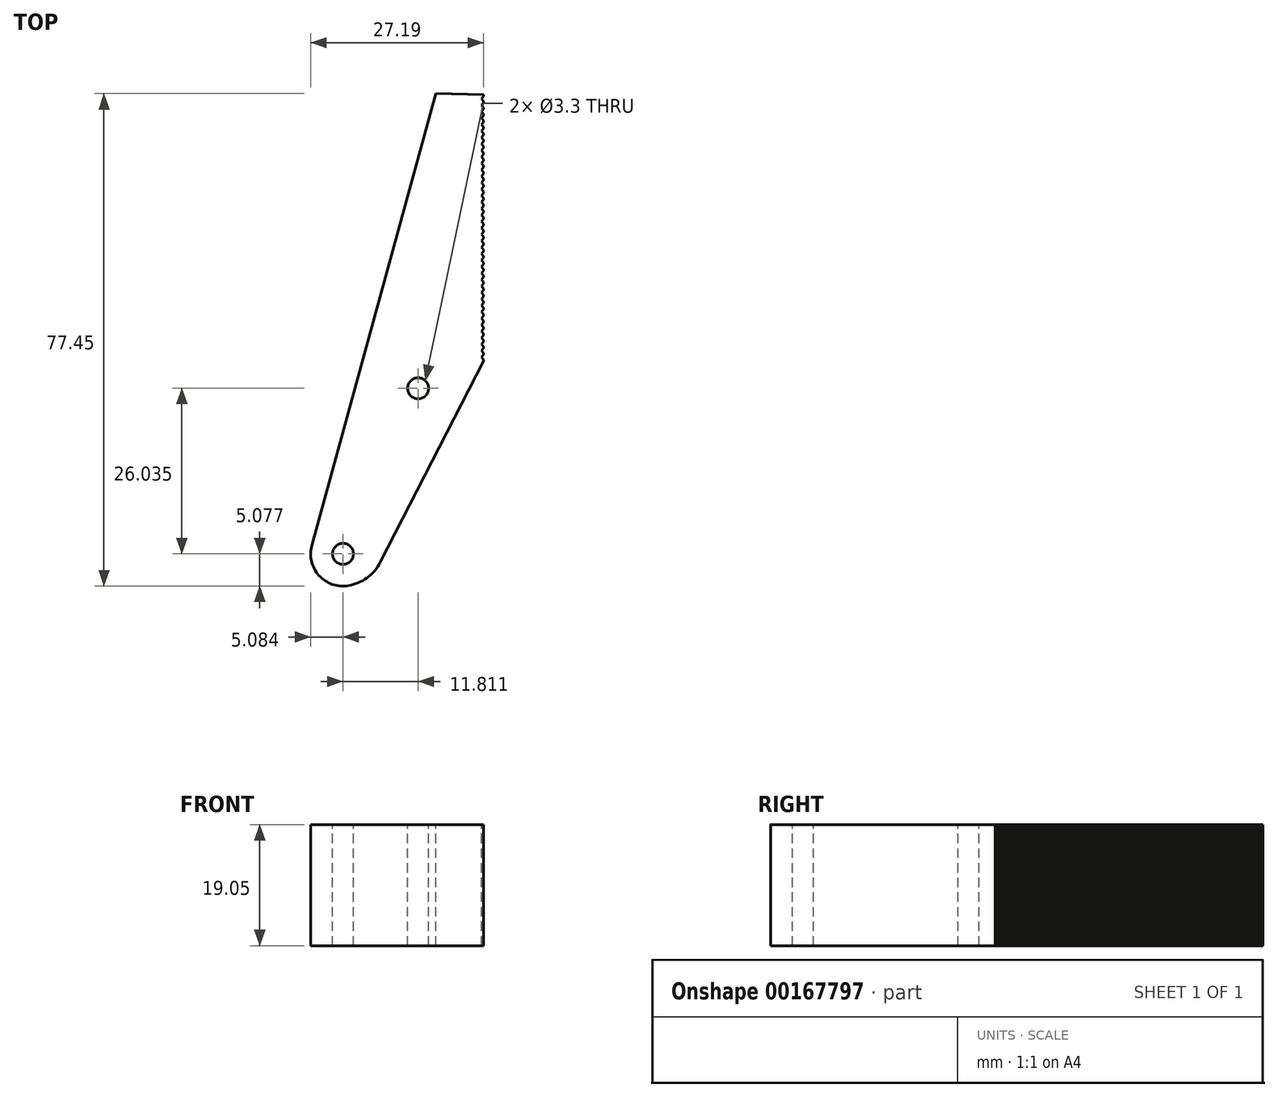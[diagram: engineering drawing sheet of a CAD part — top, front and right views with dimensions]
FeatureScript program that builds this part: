
annotation { "Feature Type Name" : "Feature", "Feature Type Description" : "" }
export const myFeature = defineFeature(function(context is Context, id is Id, definition is map)
    precondition{}
    {
        {
            var Q0;
            Q0=qCreatedBy(makeId("Top.planeOp"),FACE);
            var sketch = newSketch(context, id + "F0", { "sketchPlane" : qUnion([Q0])});
            skLineSegment(sketch, "E0", {"start": v(19.05, 0) * mm, "end": v(19.05, 63.5) * mm});
            skLineSegment(sketch, "E1", {"start": v(19.05, 0) * mm, "end": v(2.8, -31.63) * mm});
            skLineSegment(sketch, "E2", {"start": v(19.05, 63.5) * mm, "end": v(17.46, 63.5) * mm});
            skLineSegment(sketch, "E3", {"start": v(17.46, 63.5) * mm, "end": v(0, 0) * mm});
            skLineSegment(sketch, "E4", {"start": v(0, 0) * mm, "end": v(-8.94, -32.52) * mm});
            skArc(sketch, "E5", {"start": v(-8.94, -32.52) * mm, "mid": v(-2.82, -35.36) * mm, "end": v(2.8, -31.63) * mm});
            skSolve(sketch);
        }
        {
            var Q0;
            Q0 = qSketchRegion(id + "F0", true);
            extrude(context, id + "F1", {"entities" : qUnion([Q0]), "depth" : 19.05 * mm});
        }
        {
            var Q0;
            Q0=makeQuery(id+"F1.opExtrude","CAP_FACE",FACE,{"disambiguationData":[OSD([sQuery(id+"F0.wireOp",EDGE,"E0"),sQuery(id+"F0.wireOp",EDGE,"V7W4c1gP-l52r-vqxn-igbG-do98eLeIA0Zb"),sQuery(id+"F0.wireOp",EDGE,"MUQwh4st-e7uD-OgjB-epZt-JrECyby666Zu"),sQuery(id+"F0.wireOp",EDGE,"E1"),sQuery(id+"F0.wireOp",EDGE,"YxZZfRpB-2lz4-PjBK-BrxY-fdydKXbAcn2m")])],"isStart":false});
            var sketch = newSketch(context, id + "F2", { "sketchPlane" : qUnion([Q0])});
            skLineSegment(sketch, "E6", {"start": v(19.05, 0.25) * mm, "end": v(18.71, 0.64) * mm});
            skLineSegment(sketch, "E7", {"start": v(18.71, 0.64) * mm, "end": v(19.05, 1.02) * mm});
            skLineSegment(sketch, "E8", {"start": v(19.05, 1.02) * mm, "end": v(19.05, 0.25) * mm});
            skLineSegment(sketch, "E9.0.1.0", {"start": v(18.71, 1.65) * mm, "end": v(19.05, 2.03) * mm});
            skLineSegment(sketch, "E9.0.1.1", {"start": v(19.05, 2.03) * mm, "end": v(19.05, 1.27) * mm});
            skLineSegment(sketch, "E9.0.1.2", {"start": v(19.05, 1.27) * mm, "end": v(18.71, 1.65) * mm});
            skLineSegment(sketch, "E9.0.2.0", {"start": v(18.71, 2.67) * mm, "end": v(19.05, 3.05) * mm});
            skLineSegment(sketch, "E9.0.2.1", {"start": v(19.05, 3.05) * mm, "end": v(19.05, 2.29) * mm});
            skLineSegment(sketch, "E9.0.2.2", {"start": v(19.05, 2.29) * mm, "end": v(18.71, 2.67) * mm});
            skLineSegment(sketch, "E9.0.3.0", {"start": v(18.71, 3.68) * mm, "end": v(19.05, 4.06) * mm});
            skLineSegment(sketch, "E9.0.3.1", {"start": v(19.05, 4.06) * mm, "end": v(19.05, 3.3) * mm});
            skLineSegment(sketch, "E9.0.3.2", {"start": v(19.05, 3.3) * mm, "end": v(18.71, 3.68) * mm});
            skLineSegment(sketch, "E9.0.4.0", {"start": v(18.71, 4.7) * mm, "end": v(19.05, 5.08) * mm});
            skLineSegment(sketch, "E9.0.4.1", {"start": v(19.05, 5.08) * mm, "end": v(19.05, 4.32) * mm});
            skLineSegment(sketch, "E9.0.4.2", {"start": v(19.05, 4.32) * mm, "end": v(18.71, 4.7) * mm});
            skLineSegment(sketch, "E9.0.5.0", {"start": v(18.71, 5.72) * mm, "end": v(19.05, 6.1) * mm});
            skLineSegment(sketch, "E9.0.5.1", {"start": v(19.05, 6.1) * mm, "end": v(19.05, 5.33) * mm});
            skLineSegment(sketch, "E9.0.5.2", {"start": v(19.05, 5.33) * mm, "end": v(18.71, 5.72) * mm});
            skLineSegment(sketch, "E9.0.6.0", {"start": v(18.71, 6.73) * mm, "end": v(19.05, 7.11) * mm});
            skLineSegment(sketch, "E9.0.6.1", {"start": v(19.05, 7.11) * mm, "end": v(19.05, 6.35) * mm});
            skLineSegment(sketch, "E9.0.6.2", {"start": v(19.05, 6.35) * mm, "end": v(18.71, 6.73) * mm});
            skLineSegment(sketch, "E9.0.7.0", {"start": v(18.71, 7.75) * mm, "end": v(19.05, 8.13) * mm});
            skLineSegment(sketch, "E9.0.7.1", {"start": v(19.05, 8.13) * mm, "end": v(19.05, 7.37) * mm});
            skLineSegment(sketch, "E9.0.7.2", {"start": v(19.05, 7.37) * mm, "end": v(18.71, 7.75) * mm});
            skLineSegment(sketch, "E9.0.8.0", {"start": v(18.71, 8.76) * mm, "end": v(19.05, 9.14) * mm});
            skLineSegment(sketch, "E9.0.8.1", {"start": v(19.05, 9.14) * mm, "end": v(19.05, 8.38) * mm});
            skLineSegment(sketch, "E9.0.8.2", {"start": v(19.05, 8.38) * mm, "end": v(18.71, 8.76) * mm});
            skLineSegment(sketch, "E9.0.9.0", {"start": v(18.71, 9.78) * mm, "end": v(19.05, 10.16) * mm});
            skLineSegment(sketch, "E9.0.9.1", {"start": v(19.05, 10.16) * mm, "end": v(19.05, 9.4) * mm});
            skLineSegment(sketch, "E9.0.9.2", {"start": v(19.05, 9.4) * mm, "end": v(18.71, 9.78) * mm});
            skLineSegment(sketch, "E9.0.10.0", {"start": v(18.71, 10.8) * mm, "end": v(19.05, 11.18) * mm});
            skLineSegment(sketch, "E9.0.10.1", {"start": v(19.05, 11.18) * mm, "end": v(19.05, 10.41) * mm});
            skLineSegment(sketch, "E9.0.10.2", {"start": v(19.05, 10.41) * mm, "end": v(18.71, 10.8) * mm});
            skLineSegment(sketch, "E9.direction1", {"start": v(19.05, 0.25) * mm, "end": v(44.45, 0.25) * mm, "construction": true});
            skLineSegment(sketch, "E9.direction2", {"start": v(19.05, 0.25) * mm, "end": v(19.05, 1.27) * mm, "construction": true});
            skLineSegment(sketch, "E10.0.0.11", {"start": v(18.71, 11.81) * mm, "end": v(19.05, 12.2) * mm});
            skLineSegment(sketch, "E10.3.0.11", {"start": v(19.05, 12.2) * mm, "end": v(19.05, 11.43) * mm});
            skLineSegment(sketch, "E10.6.0.11", {"start": v(19.05, 11.43) * mm, "end": v(18.71, 11.81) * mm});
            skLineSegment(sketch, "E10.0.0.12", {"start": v(18.71, 12.83) * mm, "end": v(19.05, 13.2) * mm});
            skLineSegment(sketch, "E10.3.0.12", {"start": v(19.05, 13.2) * mm, "end": v(19.05, 12.45) * mm});
            skLineSegment(sketch, "E10.6.0.12", {"start": v(19.05, 12.45) * mm, "end": v(18.71, 12.83) * mm});
            skLineSegment(sketch, "E10.0.0.13", {"start": v(18.71, 13.84) * mm, "end": v(19.05, 14.22) * mm});
            skLineSegment(sketch, "E10.3.0.13", {"start": v(19.05, 14.22) * mm, "end": v(19.05, 13.46) * mm});
            skLineSegment(sketch, "E10.6.0.13", {"start": v(19.05, 13.46) * mm, "end": v(18.71, 13.84) * mm});
            skLineSegment(sketch, "E10.0.0.14", {"start": v(18.71, 14.86) * mm, "end": v(19.05, 15.24) * mm});
            skLineSegment(sketch, "E10.3.0.14", {"start": v(19.05, 15.24) * mm, "end": v(19.05, 14.48) * mm});
            skLineSegment(sketch, "E10.6.0.14", {"start": v(19.05, 14.48) * mm, "end": v(18.71, 14.86) * mm});
            skLineSegment(sketch, "E10.0.0.15", {"start": v(18.71, 15.88) * mm, "end": v(19.05, 16.26) * mm});
            skLineSegment(sketch, "E10.3.0.15", {"start": v(19.05, 16.26) * mm, "end": v(19.05, 15.5) * mm});
            skLineSegment(sketch, "E10.6.0.15", {"start": v(19.05, 15.5) * mm, "end": v(18.71, 15.88) * mm});
            skLineSegment(sketch, "E10.0.0.16", {"start": v(18.71, 16.9) * mm, "end": v(19.05, 17.27) * mm});
            skLineSegment(sketch, "E10.3.0.16", {"start": v(19.05, 17.27) * mm, "end": v(19.05, 16.51) * mm});
            skLineSegment(sketch, "E10.6.0.16", {"start": v(19.05, 16.51) * mm, "end": v(18.71, 16.9) * mm});
            skLineSegment(sketch, "E10.0.0.17", {"start": v(18.71, 17.9) * mm, "end": v(19.05, 18.29) * mm});
            skLineSegment(sketch, "E10.3.0.17", {"start": v(19.05, 18.29) * mm, "end": v(19.05, 17.53) * mm});
            skLineSegment(sketch, "E10.6.0.17", {"start": v(19.05, 17.53) * mm, "end": v(18.71, 17.9) * mm});
            skLineSegment(sketch, "E10.0.0.18", {"start": v(18.71, 18.92) * mm, "end": v(19.05, 19.3) * mm});
            skLineSegment(sketch, "E10.3.0.18", {"start": v(19.05, 19.3) * mm, "end": v(19.05, 18.54) * mm});
            skLineSegment(sketch, "E10.6.0.18", {"start": v(19.05, 18.54) * mm, "end": v(18.71, 18.92) * mm});
            skLineSegment(sketch, "E10.0.0.19", {"start": v(18.71, 19.94) * mm, "end": v(19.05, 20.32) * mm});
            skLineSegment(sketch, "E10.3.0.19", {"start": v(19.05, 20.32) * mm, "end": v(19.05, 19.56) * mm});
            skLineSegment(sketch, "E10.6.0.19", {"start": v(19.05, 19.56) * mm, "end": v(18.71, 19.94) * mm});
            skLineSegment(sketch, "E10.0.0.20", {"start": v(18.71, 20.96) * mm, "end": v(19.05, 21.34) * mm});
            skLineSegment(sketch, "E10.3.0.20", {"start": v(19.05, 21.34) * mm, "end": v(19.05, 20.57) * mm});
            skLineSegment(sketch, "E10.6.0.20", {"start": v(19.05, 20.57) * mm, "end": v(18.71, 20.96) * mm});
            skLineSegment(sketch, "E10.0.0.21", {"start": v(18.71, 21.97) * mm, "end": v(19.05, 22.35) * mm});
            skLineSegment(sketch, "E10.3.0.21", {"start": v(19.05, 22.35) * mm, "end": v(19.05, 21.6) * mm});
            skLineSegment(sketch, "E10.6.0.21", {"start": v(19.05, 21.6) * mm, "end": v(18.71, 21.97) * mm});
            skLineSegment(sketch, "E10.0.0.22", {"start": v(18.71, 22.99) * mm, "end": v(19.05, 23.37) * mm});
            skLineSegment(sketch, "E10.3.0.22", {"start": v(19.05, 23.37) * mm, "end": v(19.05, 22.6) * mm});
            skLineSegment(sketch, "E10.6.0.22", {"start": v(19.05, 22.6) * mm, "end": v(18.71, 22.99) * mm});
            skLineSegment(sketch, "E10.0.0.23", {"start": v(18.71, 24) * mm, "end": v(19.05, 24.38) * mm});
            skLineSegment(sketch, "E10.3.0.23", {"start": v(19.05, 24.38) * mm, "end": v(19.05, 23.62) * mm});
            skLineSegment(sketch, "E10.6.0.23", {"start": v(19.05, 23.62) * mm, "end": v(18.71, 24) * mm});
            skLineSegment(sketch, "E10.0.0.24", {"start": v(18.71, 25.02) * mm, "end": v(19.05, 25.4) * mm});
            skLineSegment(sketch, "E10.3.0.24", {"start": v(19.05, 25.4) * mm, "end": v(19.05, 24.64) * mm});
            skLineSegment(sketch, "E10.6.0.24", {"start": v(19.05, 24.64) * mm, "end": v(18.71, 25.02) * mm});
            skLineSegment(sketch, "E10.0.0.25", {"start": v(18.71, 26.04) * mm, "end": v(19.05, 26.42) * mm});
            skLineSegment(sketch, "E10.3.0.25", {"start": v(19.05, 26.42) * mm, "end": v(19.05, 25.65) * mm});
            skLineSegment(sketch, "E10.6.0.25", {"start": v(19.05, 25.65) * mm, "end": v(18.71, 26.04) * mm});
            skLineSegment(sketch, "E10.0.0.26", {"start": v(18.71, 27.05) * mm, "end": v(19.05, 27.43) * mm});
            skLineSegment(sketch, "E10.3.0.26", {"start": v(19.05, 27.43) * mm, "end": v(19.05, 26.67) * mm});
            skLineSegment(sketch, "E10.6.0.26", {"start": v(19.05, 26.67) * mm, "end": v(18.71, 27.05) * mm});
            skLineSegment(sketch, "E10.0.0.27", {"start": v(18.71, 28.07) * mm, "end": v(19.05, 28.45) * mm});
            skLineSegment(sketch, "E10.3.0.27", {"start": v(19.05, 28.45) * mm, "end": v(19.05, 27.69) * mm});
            skLineSegment(sketch, "E10.6.0.27", {"start": v(19.05, 27.69) * mm, "end": v(18.71, 28.07) * mm});
            skLineSegment(sketch, "E10.0.0.28", {"start": v(18.71, 29.08) * mm, "end": v(19.05, 29.46) * mm});
            skLineSegment(sketch, "E10.3.0.28", {"start": v(19.05, 29.46) * mm, "end": v(19.05, 28.7) * mm});
            skLineSegment(sketch, "E10.6.0.28", {"start": v(19.05, 28.7) * mm, "end": v(18.71, 29.08) * mm});
            skLineSegment(sketch, "E10.0.0.29", {"start": v(18.71, 30.1) * mm, "end": v(19.05, 30.48) * mm});
            skLineSegment(sketch, "E10.3.0.29", {"start": v(19.05, 30.48) * mm, "end": v(19.05, 29.72) * mm});
            skLineSegment(sketch, "E10.6.0.29", {"start": v(19.05, 29.72) * mm, "end": v(18.71, 30.1) * mm});
            skLineSegment(sketch, "E10.0.0.30", {"start": v(18.71, 31.12) * mm, "end": v(19.05, 31.5) * mm});
            skLineSegment(sketch, "E10.3.0.30", {"start": v(19.05, 31.5) * mm, "end": v(19.05, 30.73) * mm});
            skLineSegment(sketch, "E10.6.0.30", {"start": v(19.05, 30.73) * mm, "end": v(18.71, 31.12) * mm});
            skLineSegment(sketch, "E10.0.0.31", {"start": v(18.71, 32.13) * mm, "end": v(19.05, 32.51) * mm});
            skLineSegment(sketch, "E10.3.0.31", {"start": v(19.05, 32.51) * mm, "end": v(19.05, 31.75) * mm});
            skLineSegment(sketch, "E10.6.0.31", {"start": v(19.05, 31.75) * mm, "end": v(18.71, 32.13) * mm});
            skLineSegment(sketch, "E10.0.0.32", {"start": v(18.71, 33.15) * mm, "end": v(19.05, 33.53) * mm});
            skLineSegment(sketch, "E10.3.0.32", {"start": v(19.05, 33.53) * mm, "end": v(19.05, 32.77) * mm});
            skLineSegment(sketch, "E10.6.0.32", {"start": v(19.05, 32.77) * mm, "end": v(18.71, 33.15) * mm});
            skLineSegment(sketch, "E10.0.0.33", {"start": v(18.71, 34.16) * mm, "end": v(19.05, 34.54) * mm});
            skLineSegment(sketch, "E10.3.0.33", {"start": v(19.05, 34.54) * mm, "end": v(19.05, 33.78) * mm});
            skLineSegment(sketch, "E10.6.0.33", {"start": v(19.05, 33.78) * mm, "end": v(18.71, 34.16) * mm});
            skLineSegment(sketch, "E10.0.0.34", {"start": v(18.71, 35.18) * mm, "end": v(19.05, 35.56) * mm});
            skLineSegment(sketch, "E10.3.0.34", {"start": v(19.05, 35.56) * mm, "end": v(19.05, 34.8) * mm});
            skLineSegment(sketch, "E10.6.0.34", {"start": v(19.05, 34.8) * mm, "end": v(18.71, 35.18) * mm});
            skLineSegment(sketch, "E10.0.0.35", {"start": v(18.71, 36.2) * mm, "end": v(19.05, 36.58) * mm});
            skLineSegment(sketch, "E10.3.0.35", {"start": v(19.05, 36.58) * mm, "end": v(19.05, 35.81) * mm});
            skLineSegment(sketch, "E10.6.0.35", {"start": v(19.05, 35.81) * mm, "end": v(18.71, 36.2) * mm});
            skLineSegment(sketch, "E10.0.0.36", {"start": v(18.71, 37.21) * mm, "end": v(19.05, 37.6) * mm});
            skLineSegment(sketch, "E10.3.0.36", {"start": v(19.05, 37.6) * mm, "end": v(19.05, 36.83) * mm});
            skLineSegment(sketch, "E10.6.0.36", {"start": v(19.05, 36.83) * mm, "end": v(18.71, 37.21) * mm});
            skLineSegment(sketch, "E10.0.0.37", {"start": v(18.71, 38.23) * mm, "end": v(19.05, 38.6) * mm});
            skLineSegment(sketch, "E10.3.0.37", {"start": v(19.05, 38.6) * mm, "end": v(19.05, 37.85) * mm});
            skLineSegment(sketch, "E10.6.0.37", {"start": v(19.05, 37.85) * mm, "end": v(18.71, 38.23) * mm});
            skLineSegment(sketch, "E10.0.0.38", {"start": v(18.71, 39.24) * mm, "end": v(19.05, 39.62) * mm});
            skLineSegment(sketch, "E10.3.0.38", {"start": v(19.05, 39.62) * mm, "end": v(19.05, 38.86) * mm});
            skLineSegment(sketch, "E10.6.0.38", {"start": v(19.05, 38.86) * mm, "end": v(18.71, 39.24) * mm});
            skLineSegment(sketch, "E10.0.0.39", {"start": v(18.71, 40.26) * mm, "end": v(19.05, 40.64) * mm});
            skLineSegment(sketch, "E10.3.0.39", {"start": v(19.05, 40.64) * mm, "end": v(19.05, 39.88) * mm});
            skLineSegment(sketch, "E10.6.0.39", {"start": v(19.05, 39.88) * mm, "end": v(18.71, 40.26) * mm});
            skLineSegment(sketch, "E11.0.0.40", {"start": v(18.71, 41.28) * mm, "end": v(19.05, 41.66) * mm});
            skLineSegment(sketch, "E11.3.0.40", {"start": v(19.05, 41.66) * mm, "end": v(19.05, 40.9) * mm});
            skLineSegment(sketch, "E11.6.0.40", {"start": v(19.05, 40.9) * mm, "end": v(18.71, 41.28) * mm});
            skLineSegment(sketch, "E11.0.0.41", {"start": v(18.71, 42.3) * mm, "end": v(19.05, 42.67) * mm});
            skLineSegment(sketch, "E11.3.0.41", {"start": v(19.05, 42.67) * mm, "end": v(19.05, 41.91) * mm});
            skLineSegment(sketch, "E11.6.0.41", {"start": v(19.05, 41.91) * mm, "end": v(18.71, 42.3) * mm});
            skLineSegment(sketch, "E11.0.0.42", {"start": v(18.71, 43.3) * mm, "end": v(19.05, 43.69) * mm});
            skLineSegment(sketch, "E11.3.0.42", {"start": v(19.05, 43.69) * mm, "end": v(19.05, 42.93) * mm});
            skLineSegment(sketch, "E11.6.0.42", {"start": v(19.05, 42.93) * mm, "end": v(18.71, 43.3) * mm});
            skLineSegment(sketch, "E11.0.0.43", {"start": v(18.71, 44.32) * mm, "end": v(19.05, 44.7) * mm});
            skLineSegment(sketch, "E11.3.0.43", {"start": v(19.05, 44.7) * mm, "end": v(19.05, 43.94) * mm});
            skLineSegment(sketch, "E11.6.0.43", {"start": v(19.05, 43.94) * mm, "end": v(18.71, 44.32) * mm});
            skLineSegment(sketch, "E11.0.0.44", {"start": v(18.71, 45.34) * mm, "end": v(19.05, 45.72) * mm});
            skLineSegment(sketch, "E11.3.0.44", {"start": v(19.05, 45.72) * mm, "end": v(19.05, 44.96) * mm});
            skLineSegment(sketch, "E11.6.0.44", {"start": v(19.05, 44.96) * mm, "end": v(18.71, 45.34) * mm});
            skLineSegment(sketch, "E11.0.0.45", {"start": v(18.71, 46.36) * mm, "end": v(19.05, 46.74) * mm});
            skLineSegment(sketch, "E11.3.0.45", {"start": v(19.05, 46.74) * mm, "end": v(19.05, 45.97) * mm});
            skLineSegment(sketch, "E11.6.0.45", {"start": v(19.05, 45.97) * mm, "end": v(18.71, 46.36) * mm});
            skLineSegment(sketch, "E11.0.0.46", {"start": v(18.71, 47.37) * mm, "end": v(19.05, 47.75) * mm});
            skLineSegment(sketch, "E11.3.0.46", {"start": v(19.05, 47.75) * mm, "end": v(19.05, 47) * mm});
            skLineSegment(sketch, "E11.6.0.46", {"start": v(19.05, 47) * mm, "end": v(18.71, 47.37) * mm});
            skLineSegment(sketch, "E11.0.0.47", {"start": v(18.71, 48.39) * mm, "end": v(19.05, 48.77) * mm});
            skLineSegment(sketch, "E11.3.0.47", {"start": v(19.05, 48.77) * mm, "end": v(19.05, 48) * mm});
            skLineSegment(sketch, "E11.6.0.47", {"start": v(19.05, 48) * mm, "end": v(18.71, 48.39) * mm});
            skLineSegment(sketch, "E11.0.0.48", {"start": v(18.71, 49.4) * mm, "end": v(19.05, 49.78) * mm});
            skLineSegment(sketch, "E11.3.0.48", {"start": v(19.05, 49.78) * mm, "end": v(19.05, 49.02) * mm});
            skLineSegment(sketch, "E11.6.0.48", {"start": v(19.05, 49.02) * mm, "end": v(18.71, 49.4) * mm});
            skLineSegment(sketch, "E11.0.0.49", {"start": v(18.71, 50.42) * mm, "end": v(19.05, 50.8) * mm});
            skLineSegment(sketch, "E11.3.0.49", {"start": v(19.05, 50.8) * mm, "end": v(19.05, 50.04) * mm});
            skLineSegment(sketch, "E11.6.0.49", {"start": v(19.05, 50.04) * mm, "end": v(18.71, 50.42) * mm});
            skLineSegment(sketch, "E11.0.0.50", {"start": v(18.71, 51.44) * mm, "end": v(19.05, 51.82) * mm});
            skLineSegment(sketch, "E11.3.0.50", {"start": v(19.05, 51.82) * mm, "end": v(19.05, 51.05) * mm});
            skLineSegment(sketch, "E11.6.0.50", {"start": v(19.05, 51.05) * mm, "end": v(18.71, 51.44) * mm});
            skLineSegment(sketch, "E11.0.0.51", {"start": v(18.71, 52.45) * mm, "end": v(19.05, 52.83) * mm});
            skLineSegment(sketch, "E11.3.0.51", {"start": v(19.05, 52.83) * mm, "end": v(19.05, 52.07) * mm});
            skLineSegment(sketch, "E11.6.0.51", {"start": v(19.05, 52.07) * mm, "end": v(18.71, 52.45) * mm});
            skLineSegment(sketch, "E11.0.0.52", {"start": v(18.71, 53.47) * mm, "end": v(19.05, 53.85) * mm});
            skLineSegment(sketch, "E11.3.0.52", {"start": v(19.05, 53.85) * mm, "end": v(19.05, 53.09) * mm});
            skLineSegment(sketch, "E11.6.0.52", {"start": v(19.05, 53.09) * mm, "end": v(18.71, 53.47) * mm});
            skLineSegment(sketch, "E11.0.0.53", {"start": v(18.71, 54.48) * mm, "end": v(19.05, 54.86) * mm});
            skLineSegment(sketch, "E11.3.0.53", {"start": v(19.05, 54.86) * mm, "end": v(19.05, 54.1) * mm});
            skLineSegment(sketch, "E11.6.0.53", {"start": v(19.05, 54.1) * mm, "end": v(18.71, 54.48) * mm});
            skLineSegment(sketch, "E11.0.0.54", {"start": v(18.71, 55.5) * mm, "end": v(19.05, 55.88) * mm});
            skLineSegment(sketch, "E11.3.0.54", {"start": v(19.05, 55.88) * mm, "end": v(19.05, 55.12) * mm});
            skLineSegment(sketch, "E11.6.0.54", {"start": v(19.05, 55.12) * mm, "end": v(18.71, 55.5) * mm});
            skLineSegment(sketch, "E11.0.0.55", {"start": v(18.71, 56.52) * mm, "end": v(19.05, 56.9) * mm});
            skLineSegment(sketch, "E11.3.0.55", {"start": v(19.05, 56.9) * mm, "end": v(19.05, 56.13) * mm});
            skLineSegment(sketch, "E11.6.0.55", {"start": v(19.05, 56.13) * mm, "end": v(18.71, 56.52) * mm});
            skLineSegment(sketch, "E11.0.0.56", {"start": v(18.71, 57.53) * mm, "end": v(19.05, 57.91) * mm});
            skLineSegment(sketch, "E11.3.0.56", {"start": v(19.05, 57.91) * mm, "end": v(19.05, 57.15) * mm});
            skLineSegment(sketch, "E11.6.0.56", {"start": v(19.05, 57.15) * mm, "end": v(18.71, 57.53) * mm});
            skLineSegment(sketch, "E11.0.0.57", {"start": v(18.71, 58.55) * mm, "end": v(19.05, 58.93) * mm});
            skLineSegment(sketch, "E11.3.0.57", {"start": v(19.05, 58.93) * mm, "end": v(19.05, 58.17) * mm});
            skLineSegment(sketch, "E11.6.0.57", {"start": v(19.05, 58.17) * mm, "end": v(18.71, 58.55) * mm});
            skLineSegment(sketch, "E11.0.0.58", {"start": v(18.71, 59.56) * mm, "end": v(19.05, 59.94) * mm});
            skLineSegment(sketch, "E11.3.0.58", {"start": v(19.05, 59.94) * mm, "end": v(19.05, 59.18) * mm});
            skLineSegment(sketch, "E11.6.0.58", {"start": v(19.05, 59.18) * mm, "end": v(18.71, 59.56) * mm});
            skLineSegment(sketch, "E11.0.0.59", {"start": v(18.71, 60.58) * mm, "end": v(19.05, 60.96) * mm});
            skLineSegment(sketch, "E11.3.0.59", {"start": v(19.05, 60.96) * mm, "end": v(19.05, 60.2) * mm});
            skLineSegment(sketch, "E11.6.0.59", {"start": v(19.05, 60.2) * mm, "end": v(18.71, 60.58) * mm});
            skLineSegment(sketch, "E12.0.0.60", {"start": v(18.71, 61.6) * mm, "end": v(19.05, 61.98) * mm});
            skLineSegment(sketch, "E12.3.0.60", {"start": v(19.05, 61.98) * mm, "end": v(19.05, 61.21) * mm});
            skLineSegment(sketch, "E12.6.0.60", {"start": v(19.05, 61.21) * mm, "end": v(18.71, 61.6) * mm});
            skLineSegment(sketch, "E12.0.0.61", {"start": v(18.71, 62.61) * mm, "end": v(19.05, 63) * mm});
            skLineSegment(sketch, "E12.3.0.61", {"start": v(19.05, 63) * mm, "end": v(19.05, 62.23) * mm});
            skLineSegment(sketch, "E12.6.0.61", {"start": v(19.05, 62.23) * mm, "end": v(18.71, 62.61) * mm});
            skSolve(sketch);
        }
        {
            var Q0;
            Q0 = qSketchRegion(id + "F2", true);
            var Q1;
            Q1=makeQuery(id+"F1.opExtrude","CAP_FACE",FACE,{"disambiguationData":[OSD([sQuery(id+"F0.wireOp",EDGE,"E0"),sQuery(id+"F0.wireOp",EDGE,"E1"),sQuery(id+"F0.wireOp",EDGE,"E2"),sQuery(id+"F0.wireOp",EDGE,"E3"),sQuery(id+"F0.wireOp",EDGE,"E4"),sQuery(id+"F0.wireOp",EDGE,"E5")])],"isStart":true});
            extrude(context, id + "F3", {"entities" : qUnion([Q0]), "operationType" : NewBodyOperationType.REMOVE, "endBound" : BoundingType.UP_TO_SURFACE, "oppositeDirection" : true, "endBoundEntityFace" : qUnion([Q1]), "depth" : 25.4 * mm});
        }
        {
            var Q0;
            Q0=makeQuery(id+"F1.opExtrude","SWEPT_EDGE",EDGE,{"disambiguationData":[OSD([sQuery(id+"F0.wireOp",EDGE,"E4"),sQuery(id+"F0.wireOp",EDGE,"E5")])]});
            fillet(context, id + "F4", {"entities" : qUnion([Q0]), "radius" : 5.08 * mm, "tangentPropagation" : true, "allowEdgeOverflow" : false});
        }
        {
            var Q0;
            Q0=makeQuery(id+"F1.opExtrude","CAP_FACE",FACE,{"disambiguationData":[OSD([sQuery(id+"F0.wireOp",EDGE,"E0"),sQuery(id+"F0.wireOp",EDGE,"E1"),sQuery(id+"F0.wireOp",EDGE,"E2"),sQuery(id+"F0.wireOp",EDGE,"E3"),sQuery(id+"F0.wireOp",EDGE,"E4"),sQuery(id+"F0.wireOp",EDGE,"E5")])],"isStart":false});
            var sketch = newSketch(context, id + "F5", { "sketchPlane" : qUnion([Q0])});
            skCircle(sketch, "E13", {"center": v(-3.06, -30.27) * mm, "radius": 1.65 * mm});
            skCircle(sketch, "E14", {"center": v(8.75, -4.24) * mm, "radius": 1.65 * mm});
            skSolve(sketch);
        }
        {
            var Q0;
            Q0 = qSketchRegion(id + "F5", true);
            var Q1;
            Q1=makeQuery(id+"F1.opExtrude","CAP_FACE",FACE,{"disambiguationData":[OSD([sQuery(id+"F0.wireOp",EDGE,"E0"),sQuery(id+"F0.wireOp",EDGE,"E1"),sQuery(id+"F0.wireOp",EDGE,"E2"),sQuery(id+"F0.wireOp",EDGE,"E3"),sQuery(id+"F0.wireOp",EDGE,"E4"),sQuery(id+"F0.wireOp",EDGE,"E5")])],"isStart":true});
            extrude(context, id + "F6", {"entities" : qUnion([Q0]), "operationType" : NewBodyOperationType.REMOVE, "endBound" : BoundingType.UP_TO_SURFACE, "oppositeDirection" : true, "endBoundEntityFace" : qUnion([Q1]), "depth" : 25.4 * mm});
        }
        {
            var Q0;
            Q0=makeQuery(id+"F1.opExtrude","CAP_FACE",FACE,{"disambiguationData":[OSD([sQuery(id+"F0.wireOp",EDGE,"E0"),sQuery(id+"F0.wireOp",EDGE,"E1"),sQuery(id+"F0.wireOp",EDGE,"E2"),sQuery(id+"F0.wireOp",EDGE,"E3"),sQuery(id+"F0.wireOp",EDGE,"E4"),sQuery(id+"F0.wireOp",EDGE,"E5")])],"isStart":false});
            var sketch = newSketch(context, id + "F7", { "sketchPlane" : qUnion([Q0])});
            skLineSegment(sketch, "E15", {"start": v(17.46, 63.5) * mm, "end": v(19.05, 63.5) * mm});
            skLineSegment(sketch, "E16", {"start": v(19.05, 41.91) * mm, "end": v(11.58, 42.1) * mm});
            skPoint(sketch, "E16.endSnap0", {"position": v(18.88, 42.1) * mm});
            skLineSegment(sketch, "E17", {"start": v(19.05, 41.91) * mm, "end": v(19.05, 63.5) * mm});
            skLineSegment(sketch, "E18", {"start": v(17.46, 63.5) * mm, "end": v(11.58, 42.1) * mm});
            skSolve(sketch);
        }
        {
            var Q0;
            Q0 = qSketchRegion(id + "F7", true);
            extrude(context, id + "F8", {"entities" : qUnion([Q0]), "operationType" : NewBodyOperationType.REMOVE, "endBound" : BoundingType.THROUGH_ALL, "oppositeDirection" : true, "depth" : 25.4 * mm});
        }
    });
